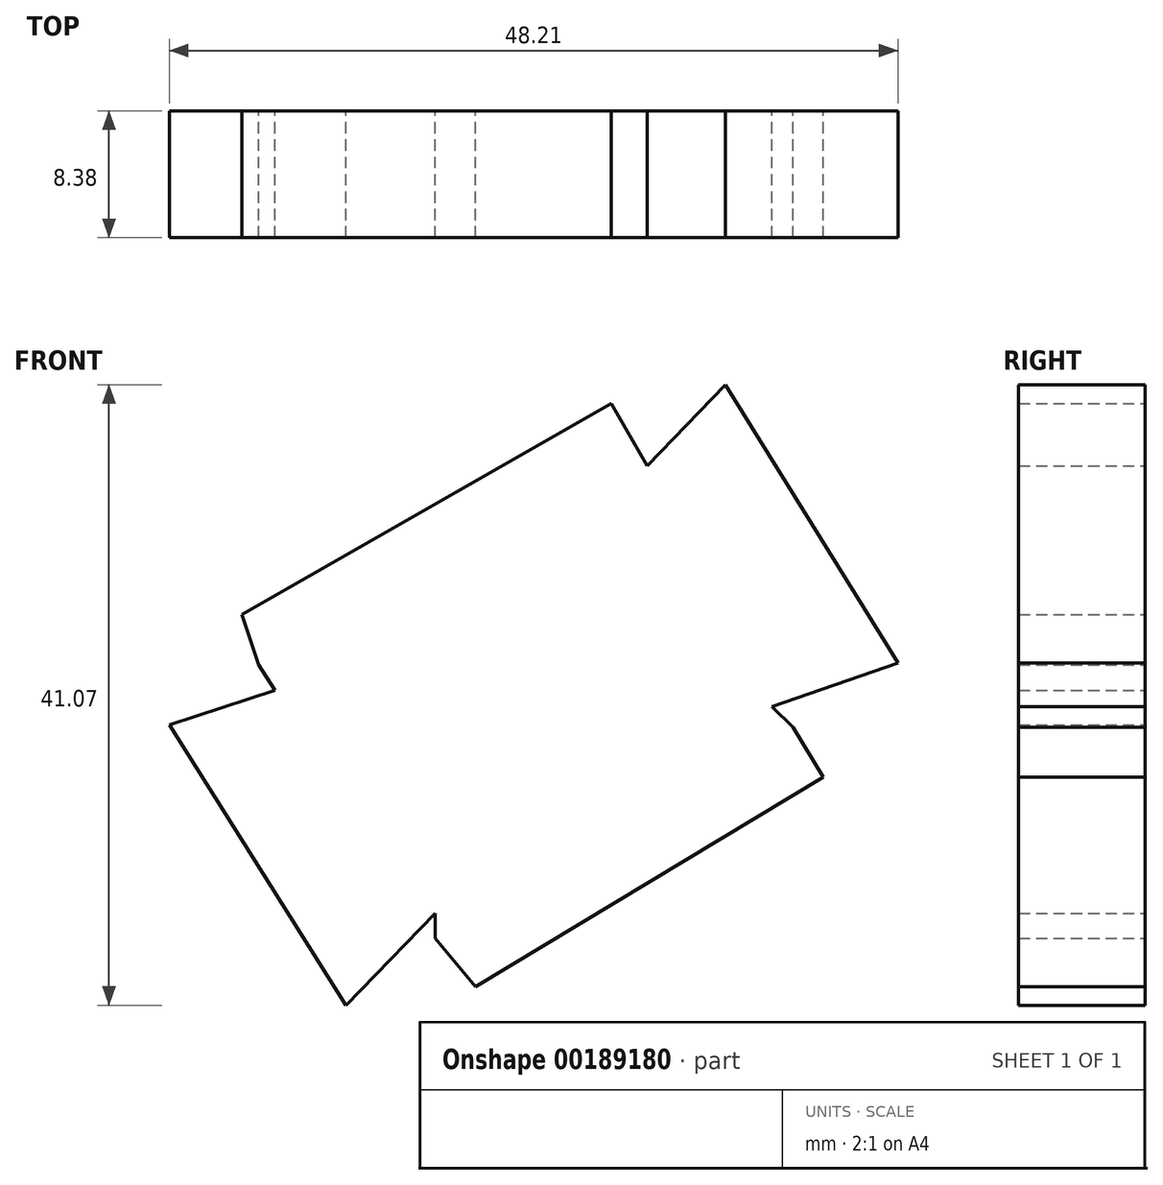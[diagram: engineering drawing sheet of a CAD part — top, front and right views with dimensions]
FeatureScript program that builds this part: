
annotation { "Feature Type Name" : "Feature", "Feature Type Description" : "" }
export const myFeature = defineFeature(function(context is Context, id is Id, definition is map)
    precondition{}
    {
        {
            var Q0;
            Q0=qCreatedBy(makeId("Front.planeOp"),FACE);
            var sketch = newSketch(context, id + "F0", { "sketchPlane" : qUnion([Q0])});
            skLineSegment(sketch, "E0", {"start": v(8.24, 16.28) * mm, "end": v(12.5, 20.67) * mm});
            skLineSegment(sketch, "E1", {"start": v(12.5, 20.67) * mm, "end": v(23.9, 2.27) * mm});
            skLineSegment(sketch, "E2", {"start": v(23.9, 2.27) * mm, "end": v(12.5, -1.72) * mm});
            skLineSegment(sketch, "E3", {"start": v(8.24, 16.28) * mm, "end": v(4.4, 12.3) * mm});
            skLineSegment(sketch, "E4", {"start": v(4.4, 12.3) * mm, "end": v(12.5, -1.72) * mm});
            skLineSegment(sketch, "E5", {"start": v(-12.64, -20.4) * mm, "end": v(-4.05, -11.54) * mm});
            skLineSegment(sketch, "E6", {"start": v(-12.64, -20.4) * mm, "end": v(-24.31, -1.85) * mm});
            skLineSegment(sketch, "E7", {"start": v(-24.31, -1.85) * mm, "end": v(-12.64, 2) * mm});
            skLineSegment(sketch, "E8", {"start": v(-12.64, 2) * mm, "end": v(-4.05, -11.54) * mm});
            skLineSegment(sketch, "E9", {"start": v(-6.73, -15.97) * mm, "end": v(-4.05, -19.16) * mm});
            skPoint(sketch, "E9.startSnap0", {"position": v(-8.35, -15.97) * mm});
            skLineSegment(sketch, "E10", {"start": v(-4.05, -19.16) * mm, "end": v(18.96, -5.29) * mm});
            skLineSegment(sketch, "E11", {"start": v(18.96, -5.29) * mm, "end": v(16.97, -2) * mm});
            skLineSegment(sketch, "E12", {"start": v(-18.4, 2.13) * mm, "end": v(-19.5, 5.47) * mm});
            skLineSegment(sketch, "E13", {"start": v(-19.5, 5.47) * mm, "end": v(4.94, 19.44) * mm});
            skLineSegment(sketch, "E14", {"start": v(4.94, 19.44) * mm, "end": v(7.3, 15.3) * mm});
            skLineSegment(sketch, "E15", {"start": v(-6.73, -14.3) * mm, "end": v(-6.73, -15.97) * mm});
            skLineSegment(sketch, "E16", {"start": v(16.97, -2) * mm, "end": v(15.57, -0.64) * mm});
            skLineSegment(sketch, "E17", {"start": v(-18.4, 2.13) * mm, "end": v(-17.34, 0.44) * mm});
            skSolve(sketch);
        }
        {
            var Q0;
            {var subQ1=sQuery(id+"F0.wireOp",EDGE,"E6");Q0=makeQuery(id+"F0.imprint","IMPRINT",FACE,{"disambiguationData":[TD([[makeQuery(id+"F0.imprint","IMPRINT",EDGE,{"derivedFrom":subQ1}),-1.0]])]});}
            var Q1;
            {var subQ6=sQuery(id+"F0.wireOp",EDGE,"E4");Q1=makeQuery(id+"F0.imprint","IMPRINT",FACE,{"disambiguationData":[TD([[makeQuery(id+"F0.imprint","IMPRINT",EDGE,{"derivedFrom":subQ6}),-1.0]])]});}
            var Q2;
            {var subQ4=sQuery(id+"F0.wireOp",EDGE,"E0");Q2=makeQuery(id+"F0.imprint","IMPRINT",FACE,{"disambiguationData":[TD([[makeQuery(id+"F0.imprint","IMPRINT",EDGE,{"derivedFrom":subQ4}),-1.0]])]});}
            extrude(context, id + "F1", {"entities" : qUnion([Q0, Q1, Q2]), "depth" : 8.38 * mm});
        }
    });
